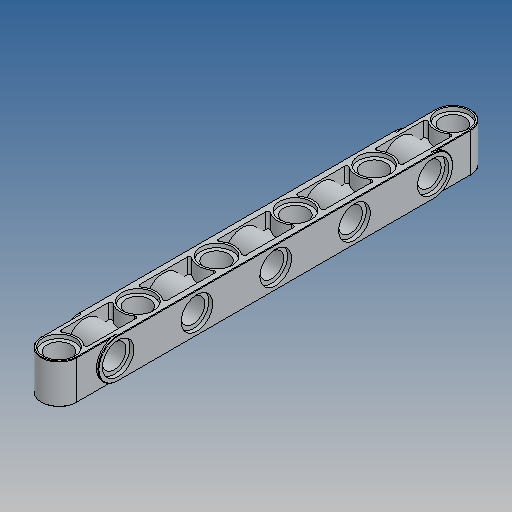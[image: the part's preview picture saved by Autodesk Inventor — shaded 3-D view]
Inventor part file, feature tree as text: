
AUTODESK INVENTOR PART (.ipt)
format: ipt  version: 2025 (Build 290162010, 162A)  size: 467,456 bytes
history: native  units: mm
features: sketch x8, extrude x7, mirror x3, fillet x2, delete_face x1, hole x1, pattern_linear x1
ambient origin geometry x8: Origin, YZ Plane, XZ Plane, XY Plane, X Axis, Y Axis, Z Axis, Center Point
bodies: Solid1 (feature_tree)
feature tree (23):
  extrude  "Extrusion1"  Depth=7.2mm
  sketch  "Sketch6"  dims[d48=80.0mm d49=6.4mm d50=4.8mm]
  extrude  "Extrusion7"  Depth=0.8mm TaperAngle=0.0deg
  extrude  "Extrusion8"  Depth=6.4mm
  mirror  "Mirror1"
  fillet  "Fillet2"  Radius=4.8mm
  mirror  "Spiegeln2"
  extrude  "Extrusion9"  Depth=0.8mm
  delete_face  "Fläche löschen1"
  fillet  "Rundung3"  Radius=50.0mm
  mirror  "Spiegeln3"
  extrude  "Extrusion10"  Depth=0.1mm
  extrude  "Extrusion11"  Depth=0.1mm
  extrude  "Extrusion12"  Depth=7.2mm TaperAngle=0.0deg
  hole  "Bohrung1"  [1 undecoded]
  pattern_linear  "Rechteckige Anordnung1"  Spacing1=0.0mm  [1 undecoded]
  sketch  "Sketch1"  dims[d14=8.0mm d15=0.0mm d32=7.2mm]
  sketch  "Skizze - Rechteckige Anordnung1"  dims[d41=0.8mm d42=0.0mm d43=3.1mm d44=0.0mm]
  sketch  "Skizze9"  dims[d51=16.0mm d52=0.8mm d53=50.0mm]
  sketch  "Skizze10"  dims[d55=16.0mm d56=10.0mm d58=10.0mm d60=0.4mm d61=0.1mm]
  sketch  "Skizze11"  dims[d63=0.4mm d64=0.0mm d65=0.1mm]
  sketch  "Skizze12"  dims[d66=7.2mm d67=0.4mm d68=0.0mm]
  sketch  "Skizze13"  dims[d69=6.4mm d70=0.8mm d71=0.0mm d72=0.8mm d73=0.0mm d74=4.8mm d75=40.0mm d76=4.0mm d77=2.0mm d78=90.0deg d79=8.0mm d80=20.594885mm d81=50.0mm d83=16.0mm d62=0.5mm]
note: 2 required parameter values undecoded (feature->parameter linkage not recoverable at this tier; creation-order binding heuristic only, values carry confidence <= 0.55)
